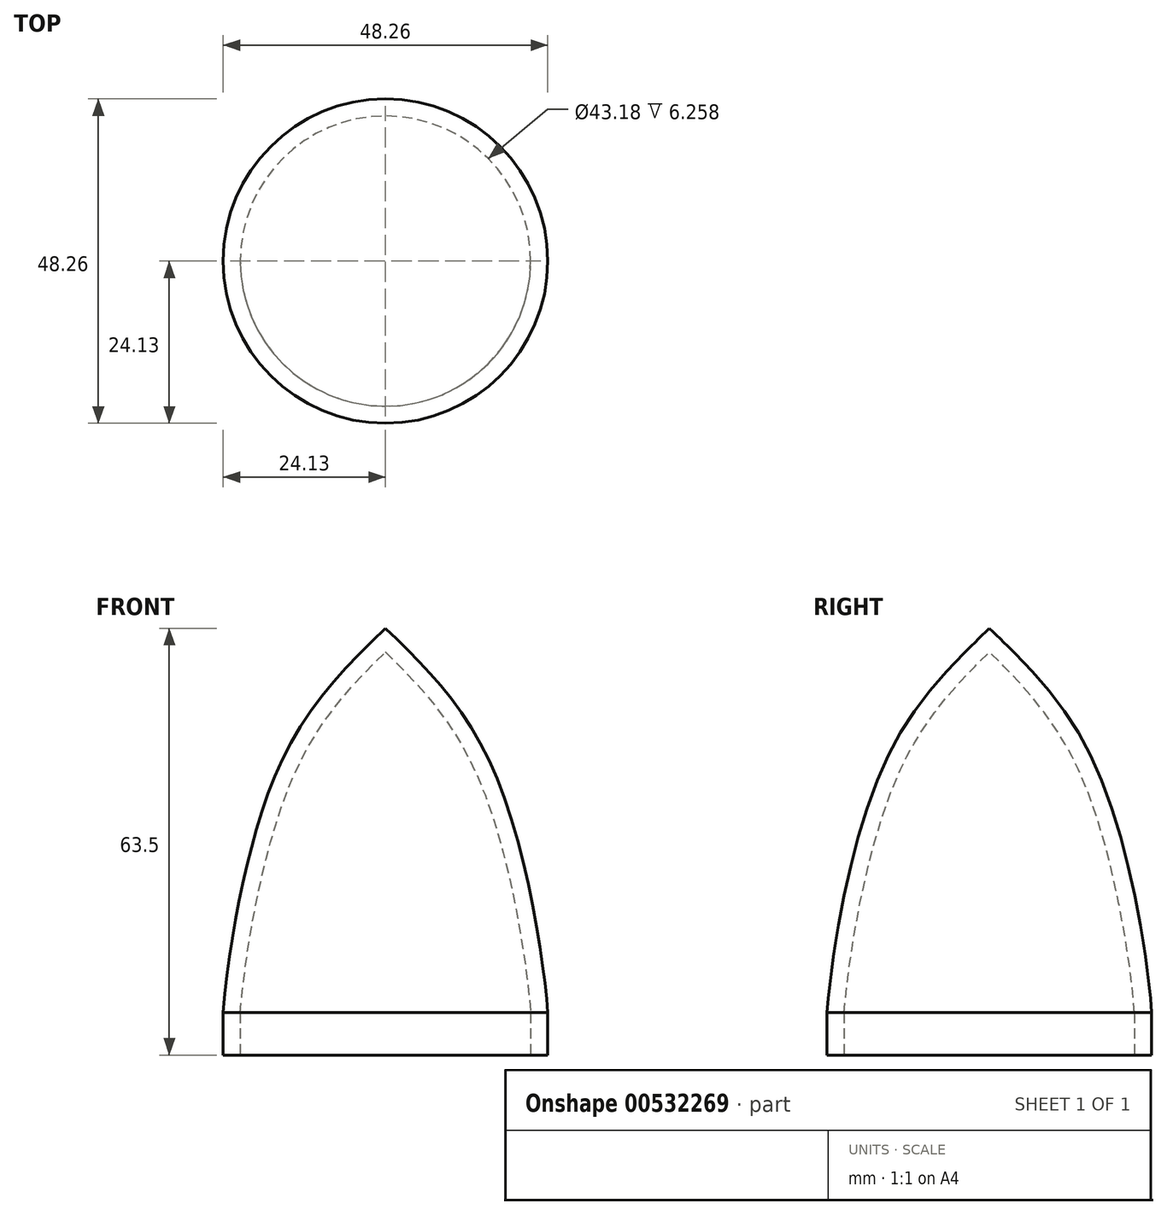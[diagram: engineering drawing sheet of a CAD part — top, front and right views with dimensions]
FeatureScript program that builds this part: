
annotation { "Feature Type Name" : "Feature", "Feature Type Description" : "" }
export const myFeature = defineFeature(function(context is Context, id is Id, definition is map)
    precondition{}
    {
        {
            var Q0;
            Q0=qCreatedBy(makeId("Front.planeOp"),FACE);
            var sketch = newSketch(context, id + "F0", { "sketchPlane" : qUnion([Q0])});
            skLineSegment(sketch, "E0.bottom", {"start": v(0, 0) * mm, "end": v(24.13, 0) * mm});
            skLineSegment(sketch, "E0.left", {"start": v(0, 0) * mm, "end": v(0, 63.5) * mm});
            skLineSegment(sketch, "E0.right", {"start": v(24.13, 0) * mm, "end": v(24.13, 6.35) * mm});
            skPoint(sketch, "E1", {"position": v(24.13, 6.35) * mm});
            skPoint(sketch, "E2", {"position": v(16.08, 42.34) * mm});
            skFitSpline(sketch, "E3", {"points": [v(0, 63.5) * mm, v(16.08, 42.34) * mm, v(24.13, 6.35) * mm, v(24.13, 0) * mm], "startDerivative": vector(47.5, -45.87) * mm, "endDerivative": vector(-1.87, -25.95) * mm});
            skSolve(sketch);
        }
        {
            var Q0;
            Q0=makeQuery(id+"F0.imprint","IMPRINT",FACE,{"disambiguationData":[TD([[makeQuery(id+"F0.imprint","IMPRINT",EDGE,{"derivedFrom":sQuery(id+"F0.wireOp",EDGE,"E0.bottom")}),1.0]])]});
            var Q1;
            Q1=sQuery(id+"F0.wireOp",EDGE,"E0.left");
            revolve(context, id + "F1", {"entities" : qUnion([Q0]), "axis" : qUnion([Q1]), "revolveType" : RevolveType.FULL});
        }
        {
            var Q0;
            Q0=makeQuery(id+"F1.opRevolve","SWEPT_FACE",FACE,{"disambiguationData":[OSD([sQuery(id+"F0.wireOp",EDGE,"E0.bottom")])]});
            shell(context, id + "F2", {"entities" : qUnion([Q0]), "thickness" : 2.54 * mm});
        }
    });
